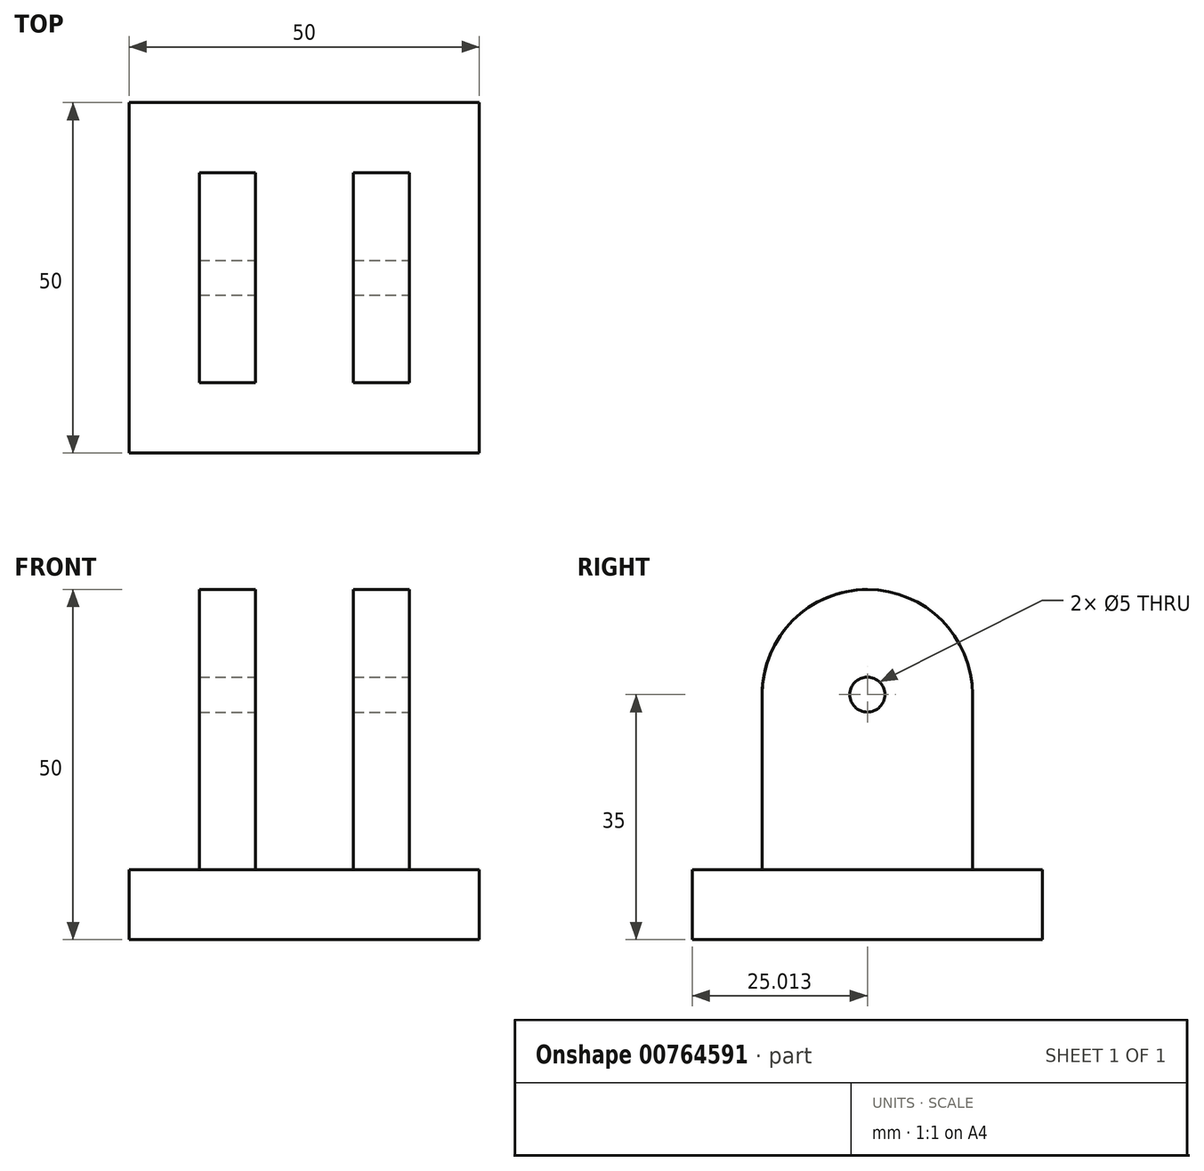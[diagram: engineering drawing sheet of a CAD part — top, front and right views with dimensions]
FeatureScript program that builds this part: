
annotation { "Feature Type Name" : "Feature", "Feature Type Description" : "" }
export const myFeature = defineFeature(function(context is Context, id is Id, definition is map)
    precondition{}
    {
        {
            var Q0;
            Q0=qCreatedBy(makeId("Top.planeOp"),FACE);
            var sketch = newSketch(context, id + "F0", { "sketchPlane" : qUnion([Q0])});
            skLineSegment(sketch, "E0.bottom", {"start": v(-23.06, 24.71) * mm, "end": v(26.94, 24.71) * mm});
            skLineSegment(sketch, "E0.top", {"start": v(-23.06, -25.29) * mm, "end": v(26.94, -25.29) * mm});
            skLineSegment(sketch, "E0.left", {"start": v(-23.06, 24.71) * mm, "end": v(-23.06, -25.29) * mm});
            skLineSegment(sketch, "E0.right", {"start": v(26.94, 24.71) * mm, "end": v(26.94, -25.29) * mm});
            skSolve(sketch);
        }
        {
            var Q0;
            Q0 = qSketchRegion(id + "F0", true);
            extrude(context, id + "F1", {"entities" : qUnion([Q0]), "depth" : 10 * mm, "offsetDistance" : 25 * mm});
        }
        {
            var Q0;
            Q0=makeQuery(id+"F1.opExtrude","CAP_FACE",FACE,{"disambiguationData":[OSD([sQuery(id+"F0.wireOp",EDGE,"E0.bottom"),sQuery(id+"F0.wireOp",EDGE,"E0.top"),sQuery(id+"F0.wireOp",EDGE,"E0.left"),sQuery(id+"F0.wireOp",EDGE,"E0.right")])],"isStart":false});
            var sketch = newSketch(context, id + "F2", { "sketchPlane" : qUnion([Q0])});
            skLineSegment(sketch, "E1.bottom", {"start": v(-13.06, 14.71) * mm, "end": v(-5.06, 14.71) * mm});
            skLineSegment(sketch, "E1.top", {"start": v(-13.06, -15.29) * mm, "end": v(-5.06, -15.29) * mm});
            skLineSegment(sketch, "E1.left", {"start": v(-13.06, 14.71) * mm, "end": v(-13.06, -15.29) * mm});
            skLineSegment(sketch, "E1.right", {"start": v(-5.06, 14.71) * mm, "end": v(-5.06, -15.29) * mm});
            skLineSegment(sketch, "E2.bottom", {"start": v(8.94, 14.72) * mm, "end": v(16.94, 14.72) * mm});
            skLineSegment(sketch, "E2.top", {"start": v(8.94, -15.28) * mm, "end": v(16.94, -15.28) * mm});
            skLineSegment(sketch, "E2.left", {"start": v(8.94, 14.72) * mm, "end": v(8.94, -15.28) * mm});
            skLineSegment(sketch, "E2.right", {"start": v(16.94, 14.72) * mm, "end": v(16.94, -15.28) * mm});
            skSolve(sketch);
        }
        {
            var Q0;
            Q0=makeQuery(id+"F2.imprint","IMPRINT",FACE,{"disambiguationData":[TD([[makeQuery(id+"F2.imprint","IMPRINT",EDGE,{"derivedFrom":sQuery(id+"F2.wireOp",EDGE,"E1.bottom")}),-1.0]])]});
            var Q1;
            Q1=makeQuery(id+"F2.imprint","IMPRINT",FACE,{"disambiguationData":[TD([[makeQuery(id+"F2.imprint","IMPRINT",EDGE,{"derivedFrom":sQuery(id+"F2.wireOp",EDGE,"E2.bottom")}),-1.0]])]});
            extrude(context, id + "F3", {"entities" : qUnion([Q0, Q1]), "operationType" : NewBodyOperationType.ADD, "depth" : 40 * mm, "offsetDistance" : 25 * mm});
        }
        {
            var Q0;
            Q0=makeQuery(id+"F3.opExtrude","CAP_EDGE",EDGE,{"disambiguationData":[OSD([sQuery(id+"F2.wireOp",EDGE,"E1.bottom")])],"isStart":false});
            var Q1;
            Q1=makeQuery(id+"F3.opExtrude","CAP_EDGE",EDGE,{"disambiguationData":[OSD([sQuery(id+"F2.wireOp",EDGE,"E1.top")])],"isStart":false});
            var Q2;
            Q2=makeQuery(id+"F3.opExtrude","CAP_EDGE",EDGE,{"disambiguationData":[OSD([sQuery(id+"F2.wireOp",EDGE,"E2.bottom")])],"isStart":false});
            var Q3;
            Q3=makeQuery(id+"F3.opExtrude","CAP_EDGE",EDGE,{"disambiguationData":[OSD([sQuery(id+"F2.wireOp",EDGE,"E2.top")])],"isStart":false});
            fillet(context, id + "F4", {"entities" : qUnion([Q0, Q1, Q2, Q3]), "radius" : 15 * mm, "tangentPropagation" : true, "allowEdgeOverflow" : false});
        }
        {
            var Q0;
            Q0=makeQuery(id+"F3.opExtrude","SWEPT_FACE",FACE,{"disambiguationData":[OSD([sQuery(id+"F2.wireOp",EDGE,"E2.right")])]});
            var sketch = newSketch(context, id + "F5", { "sketchPlane" : qUnion([Q0])});
            skCircle(sketch, "E3", {"center": v(-0.28, 35) * mm, "radius": 2.5 * mm});
            skSolve(sketch);
        }
        {
            var Q0;
            Q0=sQuery(id+"F5.wireOp",VERTEX,"E3.center");
            var Q1;
            Q1=makeQuery(id+"F1.opExtrude","SWEPT_BODY",BODY,{"disambiguationData":[OSD([sQuery(id+"F0.wireOp",EDGE,"E0.bottom"),sQuery(id+"F0.wireOp",EDGE,"E0.top"),sQuery(id+"F0.wireOp",EDGE,"E0.left"),sQuery(id+"F0.wireOp",EDGE,"E0.right")])]});
            hole(context, id + "F6", {"style" : HoleStyle.SIMPLE, "endStyle" : HoleEndStyle.THROUGH, "holeDiameter" : 5 * mm, "majorDiameter" : 5 * mm, "isTappedThrough" : true, "tappedDepth" : 12 * mm, "tapClearance" : 3, "locations" : qUnion([Q0]), "scope" : qUnion([Q1])});
        }
    });
